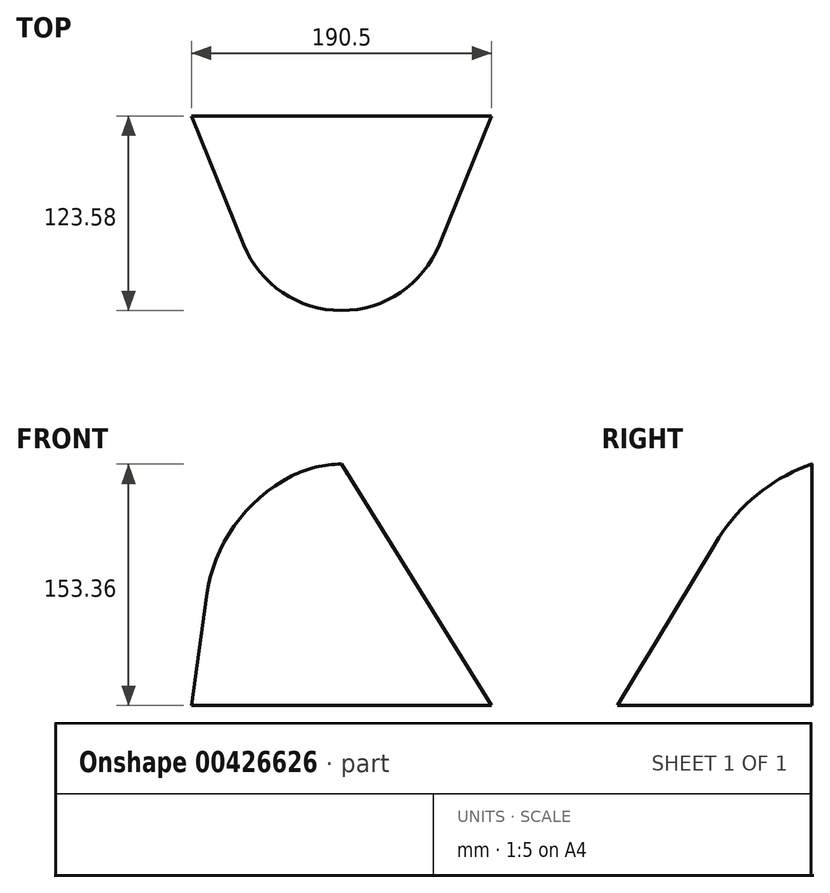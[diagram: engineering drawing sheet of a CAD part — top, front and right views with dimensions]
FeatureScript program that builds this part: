
annotation { "Feature Type Name" : "Feature", "Feature Type Description" : "" }
export const myFeature = defineFeature(function(context is Context, id is Id, definition is map)
    precondition{}
    {
        {
            var Q0;
            Q0=qCreatedBy(makeId("Front.planeOp"),FACE);
            var sketch = newSketch(context, id + "F0", { "sketchPlane" : qUnion([Q0])});
            skLineSegment(sketch, "E0", {"start": v(0, 111.3) * mm, "end": v(0, 0) * mm, "construction": true});
            skLineSegment(sketch, "E1", {"start": v(0, 0) * mm, "end": v(95.25, 0) * mm});
            skLineSegment(sketch, "E2", {"start": v(95.25, 0) * mm, "end": v(85.8, 69.13) * mm});
            skArc(sketch, "E3", {"start": v(85.8, 69.13) * mm, "mid": v(68.09, 114.03) * mm, "end": v(31.65, 145.7) * mm});
            skArc(sketch, "E4", {"start": v(31.65, 145.7) * mm, "mid": v(0, 153.36) * mm, "end": v(-31.65, 145.7) * mm});
            skArc(sketch, "E5.MirrorCS", {"start": v(-85.8, 69.13) * mm, "mid": v(-68.09, 114.03) * mm, "end": v(-31.65, 145.7) * mm});
            skLineSegment(sketch, "E6.MirrorCS", {"start": v(-95.25, 0) * mm, "end": v(-85.8, 69.13) * mm});
            skLineSegment(sketch, "E7.MirrorCS", {"start": v(0, 0) * mm, "end": v(-95.25, 0) * mm});
            skSolve(sketch);
        }
        {
            var Q0;
            Q0=qCreatedBy(makeId("Top.planeOp"),FACE);
            var sketch = newSketch(context, id + "F1", { "sketchPlane" : qUnion([Q0])});
            skLineSegment(sketch, "E8", {"start": v(-95.25, 0) * mm, "end": v(-62.12, -81.74) * mm});
            skArc(sketch, "E9", {"start": v(-62.12, -81.74) * mm, "mid": v(0, -123.58) * mm, "end": v(62.12, -81.74) * mm});
            skLineSegment(sketch, "E10", {"start": v(0, 0) * mm, "end": v(0, -123.58) * mm, "construction": true});
            skLineSegment(sketch, "E11", {"start": v(-95.25, 0) * mm, "end": v(95.25, 0) * mm});
            skLineSegment(sketch, "E12.MirrorCS", {"start": v(95.25, 0) * mm, "end": v(62.12, -81.74) * mm});
            skSolve(sketch);
        }
        {
            var Q0;
            Q0=qCreatedBy(makeId("Right.planeOp"),FACE);
            var sketch = newSketch(context, id + "F2", { "sketchPlane" : qUnion([Q0])});
            skArc(sketch, "E13", {"start": v(0, 153.36) * mm, "mid": v(-34.36, 134.32) * mm, "end": v(-60.2, 104.73) * mm});
            skLineSegment(sketch, "E14", {"start": v(-60.2, 104.73) * mm, "end": v(-123.58, 0) * mm});
            skSolve(sketch);
        }
        {
            var Q0;
            Q0=qCreatedBy(makeId("Front.planeOp"),FACE);
            var sketch = newSketch(context, id + "F3", { "sketchPlane" : qUnion([Q0])});
            skArc(sketch, "E15.0", {"start": v(0, 153.36) * mm, "mid": v(-16.28, 151.41) * mm, "end": v(-31.65, 145.7) * mm});
            skArc(sketch, "E15.1", {"start": v(-85.8, 69.13) * mm, "mid": v(-68.09, 114.03) * mm, "end": v(-31.65, 145.7) * mm});
            skLineSegment(sketch, "E15.2", {"start": v(-95.25, 0) * mm, "end": v(-85.8, 69.13) * mm});
            skSolve(sketch);
        }
        {
            var Q0;
            Q0=sQuery(id+"F0.wireOp",EDGE,"E4");
            cPoint(context, id + "F4", {"entities" : qUnion([Q0]), "parameter" : 0.5});
        }
        {
            var Q0;
            Q0=makeQuery(id+"F0.imprint","IMPRINT",FACE,{"disambiguationData":[TD([[makeQuery(id+"F0.imprint","IMPRINT",EDGE,{"derivedFrom":sQuery(id+"F0.wireOp",EDGE,"E1")}),1.0]])]});
            var Q1;
            Q1=sQuery(id+"F2.wireOp",VERTEX,"E14.end");
            var Q2;
            Q2=makeQuery(id+"F1.imprint","IMPRINT",FACE,{"disambiguationData":[TD([[makeQuery(id+"F1.imprint","IMPRINT",EDGE,{"derivedFrom":sQuery(id+"F1.wireOp",EDGE,"E8")}),1.0]])]});
            var Q3;
            Q3 = qCreatedBy(id + "F4" ,VERTEX);
            var Q4;
            Q4 = qConstructionFilter(qBodyType(qCreatedBy(id + "F2" ,EDGE), BodyType.WIRE), ConstructionObject.NO);
            var Q5;
            Q5 = qConstructionFilter(qBodyType(qCreatedBy(id + "F3" ,EDGE), BodyType.WIRE), ConstructionObject.NO);
            loft(context, id + "F5", {"bodyType" : ToolBodyType.SURFACE, "addGuides" : true, "sheetProfilesArray" : [{ "sheetProfileEntities" : qUnion([Q0]) }, { "sheetProfileEntities" : qUnion([Q1]) }], "wireProfilesArray" : [{ "wireProfileEntities" : qUnion([Q2]) }, { "wireProfileEntities" : qUnion([Q3]) }], "guidesArray" : [{ "guideEntities" : qUnion([Q4]), "guideDerivativeType" : LoftGuideDerivativeType.DEFAULT, "guideDerivativeMagnitude" : 1 }, { "guideEntities" : qUnion([Q5]), "guideDerivativeType" : LoftGuideDerivativeType.DEFAULT, "guideDerivativeMagnitude" : 1 }]});
        }
    });
